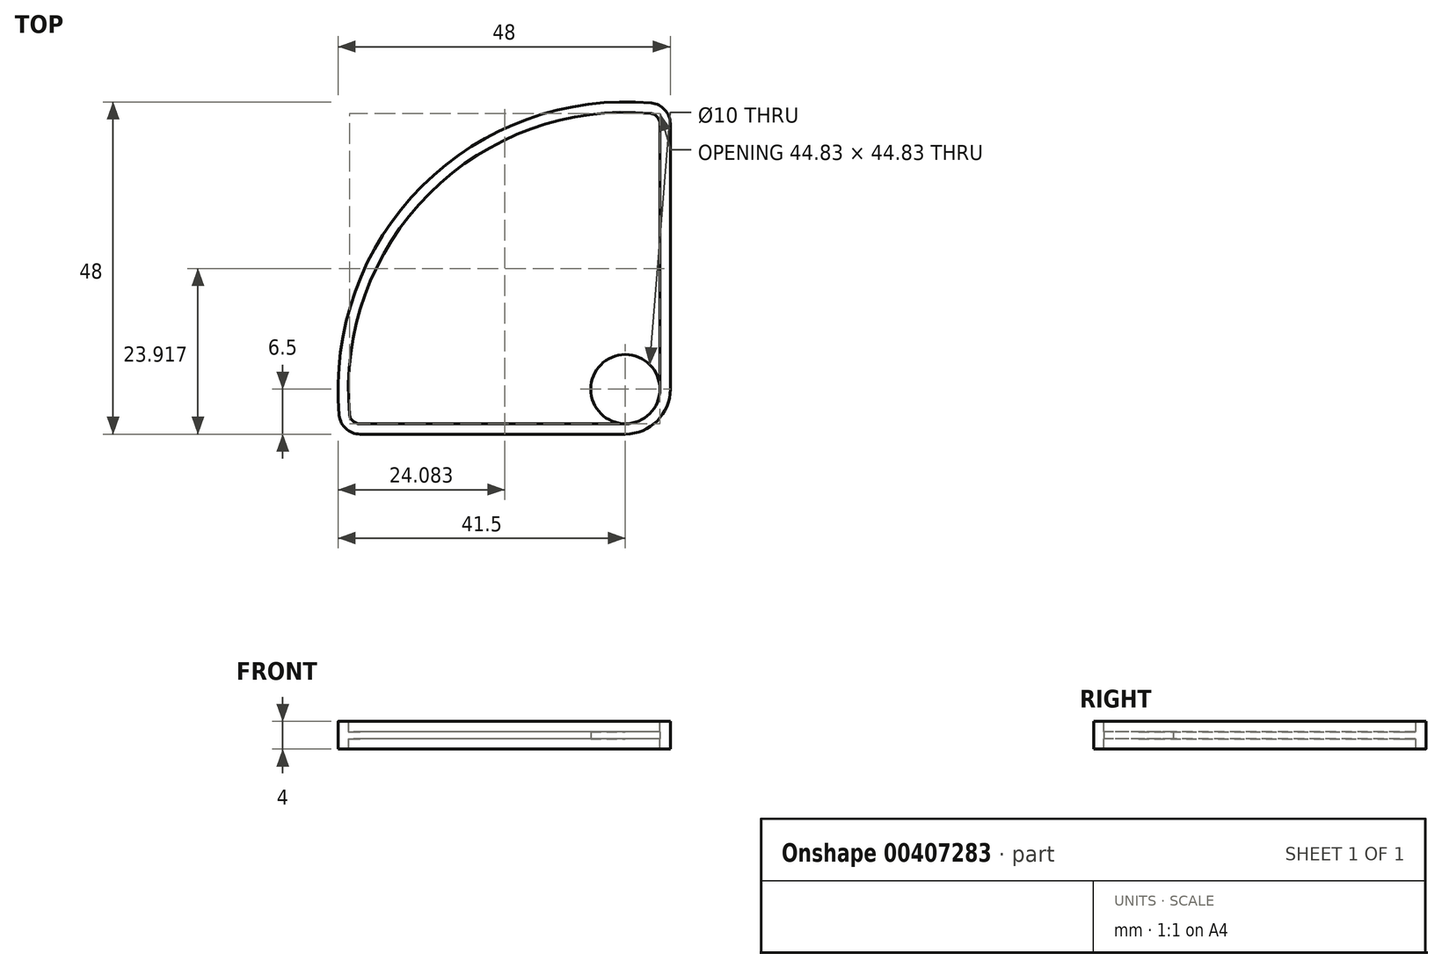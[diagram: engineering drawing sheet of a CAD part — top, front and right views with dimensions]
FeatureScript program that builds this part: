
annotation { "Feature Type Name" : "Feature", "Feature Type Description" : "" }
export const myFeature = defineFeature(function(context is Context, id is Id, definition is map)
    precondition{}
    {
        {
            var Q0;
            Q0=qCreatedBy(makeId("Top.planeOp"),FACE);
            var sketch = newSketch(context, id + "F0", { "sketchPlane" : qUnion([Q0])});
            skLineSegment(sketch, "E0", {"start": v(0, 6.5) * mm, "end": v(0, 47.49) * mm});
            skArc(sketch, "E1", {"start": v(0, 0) * mm, "mid": v(-6.5, 6.5) * mm, "end": v(-13, 0) * mm, "construction": true});
            skLineSegment(sketch, "E2", {"start": v(-13, 0) * mm, "end": v(-6.5, 0) * mm});
            skPoint(sketch, "E3.visualSharp", {"position": v(0, 0) * mm});
            skArc(sketch, "E3.filletArc", {"start": v(-6.5, 0) * mm, "mid": v(-1.9, 1.9) * mm, "end": v(0, 6.5) * mm});
            skLineSegment(sketch, "E4", {"start": v(-13, 0) * mm, "end": v(-13, 7.96) * mm, "construction": true});
            skLineSegment(sketch, "E5", {"start": v(0, 6.5) * mm, "end": v(-13, 6.5) * mm, "construction": true});
            skLineSegment(sketch, "E6", {"start": v(-6.5, 0) * mm, "end": v(-6.5, 6.5) * mm, "construction": true});
            skArc(sketch, "E7", {"start": v(-47.49, 0) * mm, "mid": v(-35.84, 35.84) * mm, "end": v(0, 47.49) * mm});
            skLineSegment(sketch, "E8", {"start": v(-13, 0) * mm, "end": v(-47.49, 0) * mm});
            skSolve(sketch);
        }
        {
            var Q0;
            Q0=makeQuery(id+"F0.imprint","IMPRINT",FACE,{"disambiguationData":[TD([[makeQuery(id+"F0.imprint","IMPRINT",EDGE,{"derivedFrom":sQuery(id+"F0.wireOp",EDGE,"E0")}),1.0]])]});
            extrude(context, id + "F1", {"entities" : qUnion([Q0]), "depth" : 4 * mm});
        }
        {
            var Q0;
            Q0=makeQuery(id+"F1.opExtrude","CAP_FACE",FACE,{"disambiguationData":[OSD([sQuery(id+"F0.wireOp",EDGE,"NLBvzQAC-VEYf-z00a-SUDr-PS6Iiug7ZcWT"),sQuery(id+"F0.wireOp",EDGE,"vp4aBCBo-WHFW-VkR4-K5s5-xs8t65EtAtv6"),sQuery(id+"F0.wireOp",EDGE,"E0")])],"isStart":false});
            var Q1;
            Q1=makeQuery(id+"F1.opExtrude","CAP_FACE",FACE,{"disambiguationData":[OSD([sQuery(id+"F0.wireOp",EDGE,"NLBvzQAC-VEYf-z00a-SUDr-PS6Iiug7ZcWT"),sQuery(id+"F0.wireOp",EDGE,"E0"),sQuery(id+"F0.wireOp",EDGE,"sY9fAtrw-aqXI-RMX0-P5VE-8Oq5YwFjua6t"),sQuery(id+"F0.wireOp",EDGE,"c47a2967-c131-48a5-880a-628ae06fc696.trimOffspring")])],"isStart":true});
            shell(context, id + "F2", {"entities" : qUnion([Q0, Q1]), "thickness" : 1.5 * mm});
        }
        {
            var Q0;
            Q0=qCreatedBy(makeId("Top.planeOp"),FACE);
            cPlane(context, id + "F3", {"entities" : qUnion([Q0]), "cplaneType" : CPlaneType.OFFSET, "offset" : 1.5 * mm, "width" : 150 * mm, "height" : 150 * mm});
        }
        {
            var Q0;
            Q0=qCreatedBy(id+"F3.planeOp",FACE);
            var sketch = newSketch(context, id + "F4", { "sketchPlane" : qUnion([Q0])});
            skLineSegment(sketch, "E9.0", {"start": v(-6.5, 1.5) * mm, "end": v(-46.19, 1.5) * mm});
            skArc(sketch, "E10.0", {"start": v(-6.5, 1.5) * mm, "mid": v(-2.96, 2.96) * mm, "end": v(-1.5, 6.5) * mm});
            skLineSegment(sketch, "E11.0", {"start": v(-1.5, 6.5) * mm, "end": v(-1.5, 46.19) * mm});
            skArc(sketch, "E12.0", {"start": v(-46.19, 1.5) * mm, "mid": v(-34.78, 34.78) * mm, "end": v(-1.5, 46.19) * mm});
            skSolve(sketch);
        }
        {
            var Q0;
            Q0=makeQuery(id+"F4.imprint","IMPRINT",FACE,{"disambiguationData":[TD([[makeQuery(id+"F4.imprint","IMPRINT",EDGE,{"derivedFrom":sQuery(id+"F4.wireOp",EDGE,"E9.0")}),-1.0]])]});
            extrude(context, id + "F5", {"entities" : qUnion([Q0]), "operationType" : NewBodyOperationType.ADD, "depth" : 1 * mm});
        }
        {
            var Q0;
            Q0=makeQuery(id+"F1.opExtrude","SWEPT_EDGE",EDGE,{"disambiguationData":[OSD([sQuery(id+"F0.wireOp",EDGE,"c47a2967-c131-48a5-880a-628ae06fc696.trimOffspring"),sQuery(id+"F0.wireOp",EDGE,"E7")])]});
            var Q1;
            Q1=makeQuery(id+"F1.opExtrude","SWEPT_EDGE",EDGE,{"disambiguationData":[OSD([sQuery(id+"F0.wireOp",EDGE,"E0"),sQuery(id+"F0.wireOp",EDGE,"E7")])]});
            fillet(context, id + "F6", {"entities" : qUnion([Q0, Q1]), "radius" : 3 * mm, "tangentPropagation" : true, "allowEdgeOverflow" : false});
        }
        {
            var Q0;
            {var subQ0=sQuery(id+"F0.wireOp",EDGE,"E7");var subQ1=sQuery(id+"F0.wireOp",EDGE,"E0");Q0=makeQuery(id+"F5.boolean.opBoolean","SPLIT",EDGE,{"disambiguationData":[TD([makeQuery(id+"F5.opExtrude","CAP_FACE",FACE,{"disambiguationData":[OSD([sQuery(id+"F4.wireOp",EDGE,"E9.0"),sQuery(id+"F4.wireOp",EDGE,"E10.0"),sQuery(id+"F4.wireOp",EDGE,"E11.0"),sQuery(id+"F4.wireOp",EDGE,"E12.0")])],"isStart":true})])],"derivedFrom":makeQuery(id+"F2.opShell","OFFSET_EDGE",EDGE,{"disambiguationData":[OSD([subQ1,subQ0])]})});}
            var Q1;
            {var subQ0=sQuery(id+"F0.wireOp",EDGE,"E8");var subQ1=sQuery(id+"F0.wireOp",EDGE,"E7");Q1=makeQuery(id+"F5.boolean.opBoolean","SPLIT",EDGE,{"disambiguationData":[TD([makeQuery(id+"F5.opExtrude","CAP_FACE",FACE,{"disambiguationData":[OSD([sQuery(id+"F4.wireOp",EDGE,"E9.0"),sQuery(id+"F4.wireOp",EDGE,"E10.0"),sQuery(id+"F4.wireOp",EDGE,"E11.0"),sQuery(id+"F4.wireOp",EDGE,"E12.0")])],"isStart":true})])],"derivedFrom":makeQuery(id+"F2.opShell","OFFSET_EDGE",EDGE,{"disambiguationData":[OSD([subQ1,subQ0])]})});}
            var Q2;
            {var subQ0=sQuery(id+"F0.wireOp",EDGE,"E8");var subQ1=sQuery(id+"F0.wireOp",EDGE,"E7");Q2=makeQuery(id+"F5.boolean.opBoolean","SPLIT",EDGE,{"disambiguationData":[TD([makeQuery(id+"F5.opExtrude","CAP_FACE",FACE,{"disambiguationData":[OSD([sQuery(id+"F4.wireOp",EDGE,"E9.0"),sQuery(id+"F4.wireOp",EDGE,"E10.0"),sQuery(id+"F4.wireOp",EDGE,"E11.0"),sQuery(id+"F4.wireOp",EDGE,"E12.0")])],"isStart":false})])],"derivedFrom":makeQuery(id+"F2.opShell","OFFSET_EDGE",EDGE,{"disambiguationData":[OSD([subQ1,subQ0])]})});}
            var Q3;
            {var subQ0=sQuery(id+"F0.wireOp",EDGE,"E7");var subQ1=sQuery(id+"F0.wireOp",EDGE,"E0");Q3=makeQuery(id+"F5.boolean.opBoolean","SPLIT",EDGE,{"disambiguationData":[TD([makeQuery(id+"F5.opExtrude","CAP_FACE",FACE,{"disambiguationData":[OSD([sQuery(id+"F4.wireOp",EDGE,"E9.0"),sQuery(id+"F4.wireOp",EDGE,"E10.0"),sQuery(id+"F4.wireOp",EDGE,"E11.0"),sQuery(id+"F4.wireOp",EDGE,"E12.0")])],"isStart":false})])],"derivedFrom":makeQuery(id+"F2.opShell","OFFSET_EDGE",EDGE,{"disambiguationData":[OSD([subQ1,subQ0])]})});}
            fillet(context, id + "F7", {"entities" : qUnion([Q0, Q1, Q2, Q3]), "radius" : 1.5 * mm, "tangentPropagation" : true, "allowEdgeOverflow" : false});
        }
        {
            var Q0;
            Q0=makeQuery(id+"F1.opExtrude","CAP_FACE",FACE,{"disambiguationData":[OSD([sQuery(id+"F0.wireOp",EDGE,"NLBvzQAC-VEYf-z00a-SUDr-PS6Iiug7ZcWT"),sQuery(id+"F0.wireOp",EDGE,"E0"),sQuery(id+"F0.wireOp",EDGE,"c47a2967-c131-48a5-880a-628ae06fc696.trimOffspring"),sQuery(id+"F0.wireOp",EDGE,"E2"),sQuery(id+"F0.wireOp",EDGE,"E3.filletArc")])],"isStart":false});
            var sketch = newSketch(context, id + "F8", { "sketchPlane" : qUnion([Q0])});
            skArc(sketch, "E13.0", {"start": v(-6.5, 1.5) * mm, "mid": v(-2.96, 2.96) * mm, "end": v(-1.5, 6.5) * mm, "construction": true});
            skCircle(sketch, "E14", {"center": v(-6.5, 6.5) * mm, "radius": 5 * mm});
            skSolve(sketch);
        }
        {
            var Q0;
            {var subQ0=sQuery(id+"F8.wireOp",EDGE,"E14");var subQ1=sQuery(id+"F0.wireOp",EDGE,"E0");var subQ2=makeQuery(id+"F8.imprint","INTERSECT",VERTEX,{"derivedFrom":[makeQuery(id+"F2.opShell","OFFSET_EDGE",EDGE,{"disambiguationData":[OSD([subQ1]),TDD([makeQuery(id+"F1.opExtrude","CAP_EDGE",EDGE,{"disambiguationData":[OSD([subQ1])],"isStart":false})])]}),subQ0]});Q0=makeQuery(id+"F8.imprint","IMPRINT",FACE,{"disambiguationData":[TD([[makeQuery(id+"F8.imprint","IMPRINT",EDGE,{"disambiguationData":[TD([[subQ2,-1.0]])],"derivedFrom":subQ0}),1.0]])]});}
            extrude(context, id + "F9", {"entities" : qUnion([Q0]), "operationType" : NewBodyOperationType.REMOVE, "oppositeDirection" : true, "depth" : 25 * mm});
        }
    });
